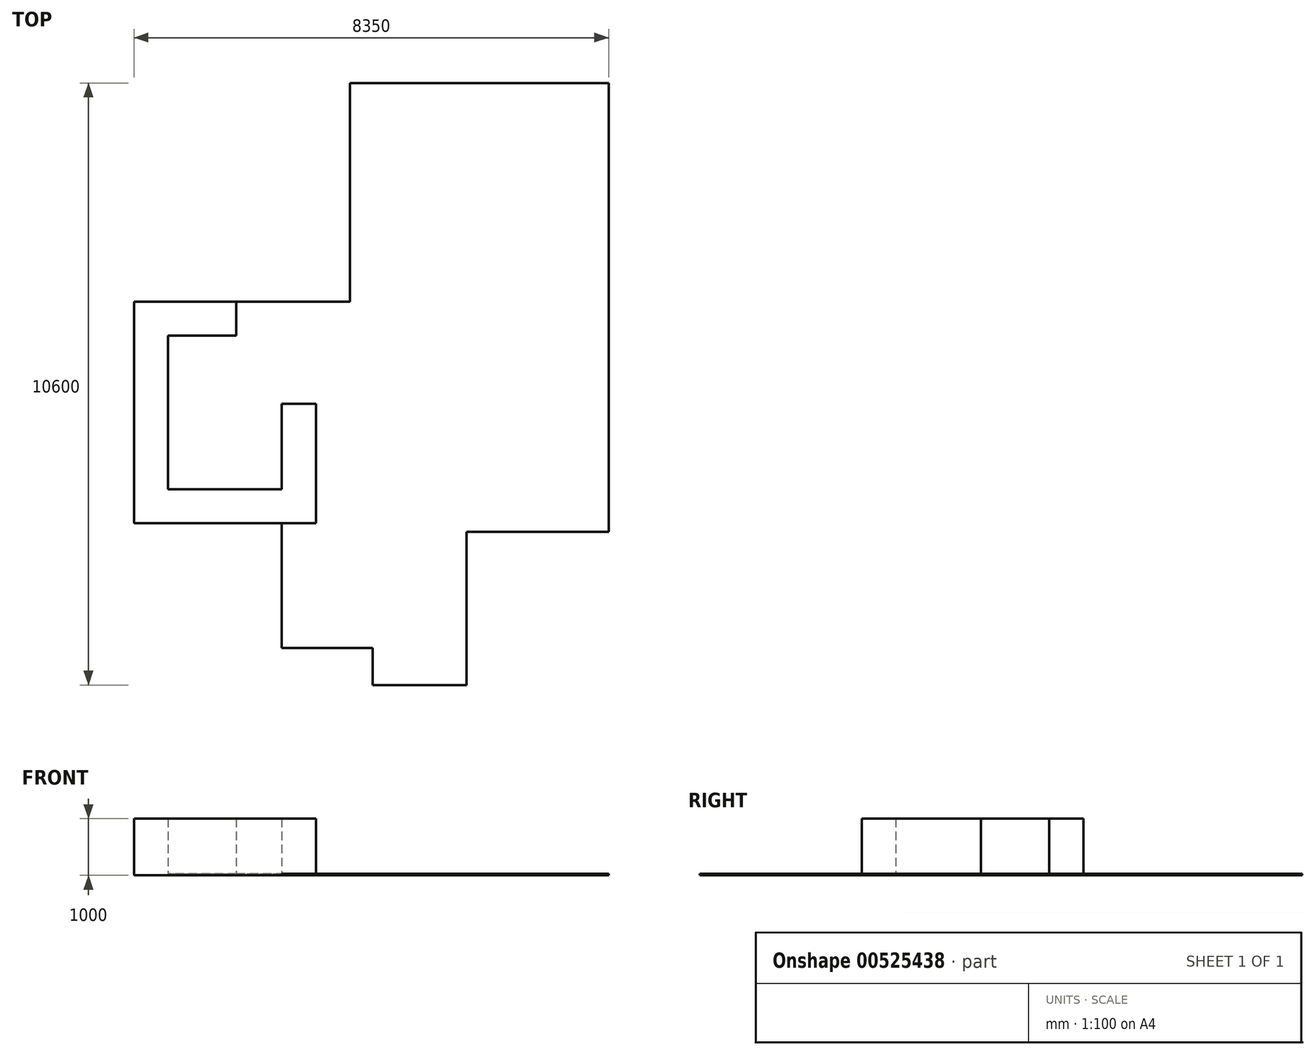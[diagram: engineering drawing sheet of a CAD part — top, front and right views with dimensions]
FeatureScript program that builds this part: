
annotation { "Feature Type Name" : "Feature", "Feature Type Description" : "" }
export const myFeature = defineFeature(function(context is Context, id is Id, definition is map)
    precondition{}
    {
        {
            var Q0;
            Q0=qCreatedBy(makeId("Top.planeOp"),FACE);
            var sketch = newSketch(context, id + "F0", { "sketchPlane" : qUnion([Q0])});
            skLineSegment(sketch, "E0", {"start": v(0, 0) * mm, "end": v(0, 7900) * mm});
            skLineSegment(sketch, "E1", {"start": v(0, 7900) * mm, "end": v(-4550, 7900) * mm});
            skLineSegment(sketch, "E2", {"start": v(-4550, 7900) * mm, "end": v(-4550, 4050) * mm});
            skLineSegment(sketch, "E3", {"start": v(-4550, 4050) * mm, "end": v(-8350, 4050) * mm});
            skLineSegment(sketch, "E4", {"start": v(-8350, 4050) * mm, "end": v(-8350, 150) * mm});
            skLineSegment(sketch, "E5", {"start": v(-8350, 150) * mm, "end": v(-5750, 150) * mm});
            skLineSegment(sketch, "E6", {"start": v(-5750, 150) * mm, "end": v(-5750, -2050) * mm});
            skLineSegment(sketch, "E7", {"start": v(-5750, -2050) * mm, "end": v(-4150, -2050) * mm});
            skLineSegment(sketch, "E8", {"start": v(-4150, -2050) * mm, "end": v(-4150, -2700) * mm});
            skLineSegment(sketch, "E9", {"start": v(-4150, -2700) * mm, "end": v(-2500, -2700) * mm});
            skLineSegment(sketch, "E10", {"start": v(-2500, -2700) * mm, "end": v(-2500, 0) * mm});
            skLineSegment(sketch, "E11", {"start": v(-2500, 0) * mm, "end": v(0, 0) * mm});
            skSolve(sketch);
        }
        {
            var Q0;
            Q0 = qSketchRegion(id + "F0", true);
            var sketch = newSketch(context, id + "F1", { "sketchPlane" : qUnion([Q0])});
            skLineSegment(sketch, "E12.0", {"start": v(-4550, 4050) * mm, "end": v(-8350, 4050) * mm});
            skLineSegment(sketch, "E13.0", {"start": v(-8350, 4050) * mm, "end": v(-8350, 150) * mm});
            skLineSegment(sketch, "E14.0", {"start": v(-8350, 150) * mm, "end": v(-5750, 150) * mm});
            skLineSegment(sketch, "E15", {"start": v(-6550, 4050) * mm, "end": v(-6550, 3450) * mm});
            skLineSegment(sketch, "E16", {"start": v(-6550, 3450) * mm, "end": v(-7750, 3450) * mm});
            skLineSegment(sketch, "E17", {"start": v(-7750, 3450) * mm, "end": v(-7750, 750) * mm});
            skLineSegment(sketch, "E18", {"start": v(-7750, 750) * mm, "end": v(-5750, 750) * mm});
            skLineSegment(sketch, "E19", {"start": v(-5750, 750) * mm, "end": v(-5750, 2250) * mm});
            skLineSegment(sketch, "E20", {"start": v(-5750, 2250) * mm, "end": v(-5150, 2250) * mm});
            skLineSegment(sketch, "E21", {"start": v(-5150, 2250) * mm, "end": v(-5150, 150) * mm});
            skLineSegment(sketch, "E22", {"start": v(-5150, 150) * mm, "end": v(-5750, 150) * mm});
            skSolve(sketch);
        }
        {
            var Q0;
            {var subQ2=sQuery(id+"F1.wireOp",EDGE,"E15");Q0=makeQuery(id+"F1.imprint","IMPRINT",FACE,{"disambiguationData":[TD([[makeQuery(id+"F1.imprint","IMPRINT",EDGE,{"derivedFrom":subQ2}),1.0]])]});}
            extrude(context, id + "F2", {"entities" : qUnion([Q0]), "depth" : 25 * mm, "offsetDistance" : 25 * mm});
        }
        {
            var Q0;
            Q0 = qSketchRegion(id + "F1", true);
            extrude(context, id + "F3", {"entities" : qUnion([Q0]), "operationType" : NewBodyOperationType.ADD, "depth" : 1000 * mm, "offsetDistance" : 25 * mm});
        }
    });
